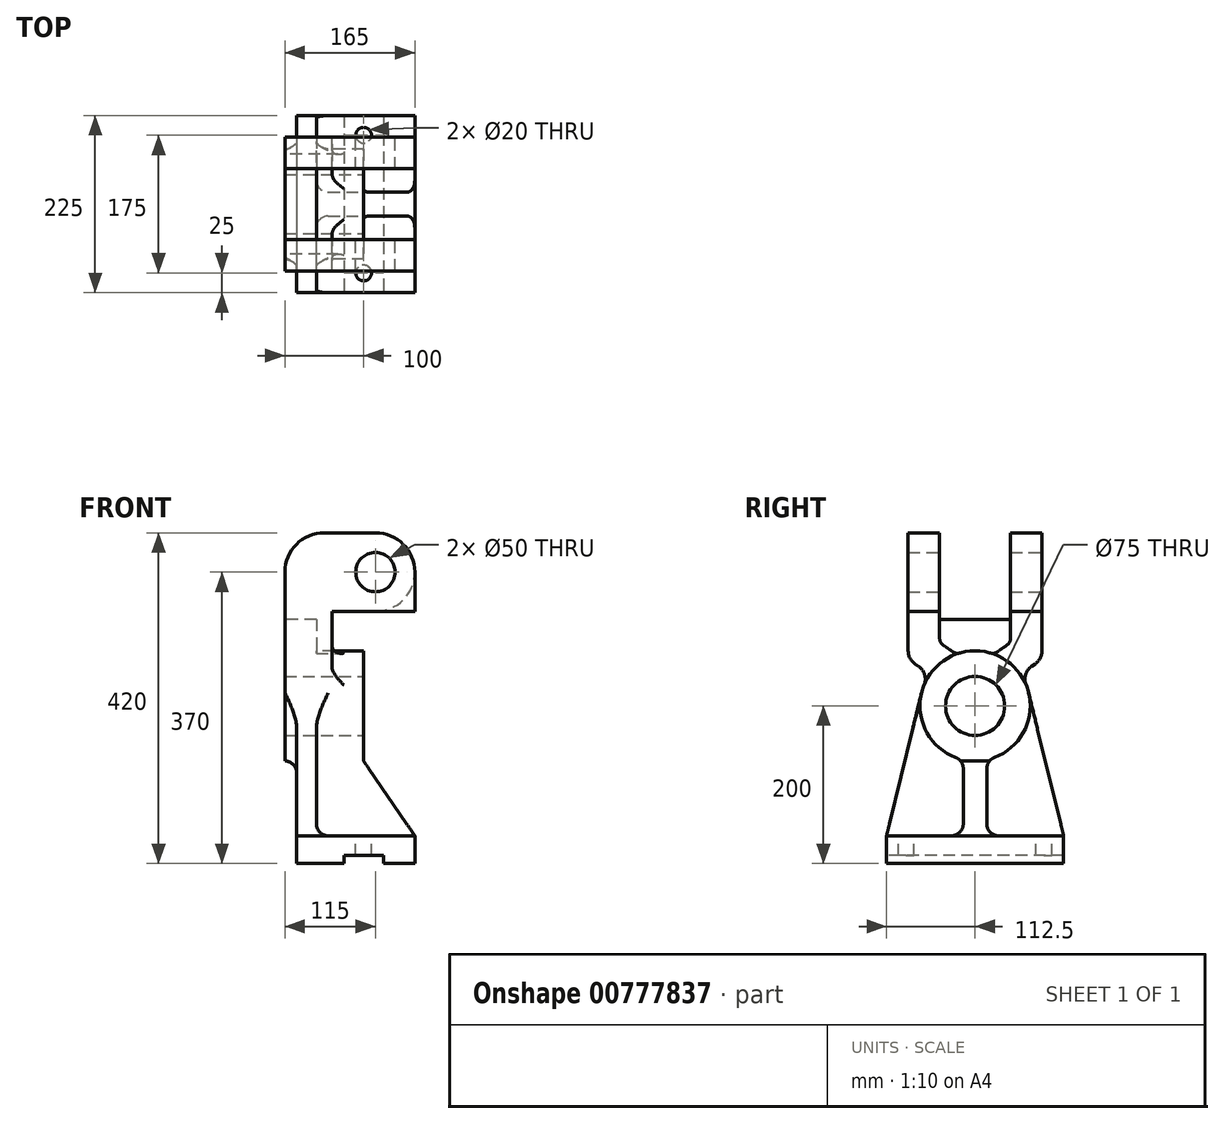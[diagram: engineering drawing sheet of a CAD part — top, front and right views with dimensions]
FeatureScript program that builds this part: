
annotation { "Feature Type Name" : "Feature", "Feature Type Description" : "" }
export const myFeature = defineFeature(function(context is Context, id is Id, definition is map)
    precondition{}
    {
        {
            var Q0;
            Q0=qCreatedBy(makeId("Right.planeOp"),FACE);
            var sketch = newSketch(context, id + "F0", { "sketchPlane" : qUnion([Q0])});
            skLineSegment(sketch, "E0", {"start": v(0, -200) * mm, "end": v(-112.5, -200) * mm});
            skLineSegment(sketch, "E1", {"start": v(-112.5, -200) * mm, "end": v(-112.5, -165) * mm});
            skLineSegment(sketch, "E2", {"start": v(-112.5, -165) * mm, "end": v(-67.99, 16.66) * mm});
            skLineSegment(sketch, "E3", {"start": v(-85, 70) * mm, "end": v(-85, 220) * mm});
            skLineSegment(sketch, "E4", {"start": v(-85, 220) * mm, "end": v(-45, 220) * mm});
            skLineSegment(sketch, "E5", {"start": v(-45, 220) * mm, "end": v(-45, 110) * mm});
            skLineSegment(sketch, "E6", {"start": v(-45, 110) * mm, "end": v(0, 110) * mm});
            skLineSegment(sketch, "E7", {"start": v(0, 110) * mm, "end": v(0, -200) * mm, "construction": true});
            skArc(sketch, "E8", {"start": v(-64.81, 26.45) * mm, "mid": v(-66.58, 21.61) * mm, "end": v(-67.99, 16.66) * mm});
            skLineSegment(sketch, "E9", {"start": v(-76.47, 53.62) * mm, "end": v(-71.86, 50.39) * mm});
            skPoint(sketch, "E10.visualSharp", {"position": v(-85, 59.59) * mm});
            skArc(sketch, "E10.filletArc", {"start": v(-85, 70) * mm, "mid": v(-82.74, 60.77) * mm, "end": v(-76.47, 53.62) * mm});
            skPoint(sketch, "E11.visualSharp", {"position": v(-57.3, 40.2) * mm});
            skArc(sketch, "E11.filletArc", {"start": v(-64.81, 26.45) * mm, "mid": v(-64.14, 39.65) * mm, "end": v(-71.86, 50.39) * mm});
            skLineSegment(sketch, "E12.MirrorCS", {"start": v(45, 110) * mm, "end": v(0, 110) * mm});
            skLineSegment(sketch, "E13.MirrorCS", {"start": v(45, 220) * mm, "end": v(45, 110) * mm});
            skLineSegment(sketch, "E14.MirrorCS", {"start": v(85, 220) * mm, "end": v(45, 220) * mm});
            skLineSegment(sketch, "E15.MirrorCS", {"start": v(85, 70) * mm, "end": v(85, 220) * mm});
            skArc(sketch, "E16.MirrorCS", {"start": v(85, 70) * mm, "mid": v(82.74, 60.77) * mm, "end": v(76.47, 53.62) * mm});
            skLineSegment(sketch, "E17.MirrorCS", {"start": v(76.47, 53.62) * mm, "end": v(71.86, 50.39) * mm});
            skArc(sketch, "E18.MirrorCS", {"start": v(64.81, 26.45) * mm, "mid": v(64.14, 39.65) * mm, "end": v(71.86, 50.39) * mm});
            skArc(sketch, "E19.MirrorCS", {"start": v(64.81, 26.45) * mm, "mid": v(66.58, 21.61) * mm, "end": v(67.99, 16.66) * mm});
            skLineSegment(sketch, "E20.MirrorCS", {"start": v(112.5, -165) * mm, "end": v(67.99, 16.66) * mm});
            skLineSegment(sketch, "E21.MirrorCS", {"start": v(112.5, -200) * mm, "end": v(112.5, -165) * mm});
            skLineSegment(sketch, "E22.MirrorCS", {"start": v(0, -200) * mm, "end": v(112.5, -200) * mm});
            skSolve(sketch);
        }
        {
            var Q0;
            Q0=makeQuery(id+"F0.imprint","IMPRINT",FACE,{"disambiguationData":[TD([[makeQuery(id+"F0.imprint","IMPRINT",EDGE,{"derivedFrom":sQuery(id+"F0.wireOp",EDGE,"E0")}),-1.0]])]});
            extrude(context, id + "F1", {"entities" : qUnion([Q0]), "depth" : 150 * mm, "offsetDistance" : 25 * mm, "hasSecondDirection" : true, "secondDirectionOppositeDirection" : true, "secondDirectionDepth" : 15 * mm});
        }
        {
            var Q0;
            Q0=makeQuery(id+"F1.opExtrude","CAP_FACE",FACE,{"disambiguationData":[OSD([sQuery(id+"F0.wireOp",EDGE,"E0"),sQuery(id+"F0.wireOp",EDGE,"E1"),sQuery(id+"F0.wireOp",EDGE,"E2"),sQuery(id+"F0.wireOp",EDGE,"E3"),sQuery(id+"F0.wireOp",EDGE,"E4"),sQuery(id+"F0.wireOp",EDGE,"E5"),sQuery(id+"F0.wireOp",EDGE,"E6"),sQuery(id+"F0.wireOp",EDGE,"E8"),sQuery(id+"F0.wireOp",EDGE,"E9"),sQuery(id+"F0.wireOp",EDGE,"E10.filletArc"),sQuery(id+"F0.wireOp",EDGE,"E11.filletArc"),sQuery(id+"F0.wireOp",EDGE,"E12.MirrorCS"),sQuery(id+"F0.wireOp",EDGE,"E13.MirrorCS"),sQuery(id+"F0.wireOp",EDGE,"E14.MirrorCS"),sQuery(id+"F0.wireOp",EDGE,"E15.MirrorCS"),sQuery(id+"F0.wireOp",EDGE,"E16.MirrorCS"),sQuery(id+"F0.wireOp",EDGE,"E17.MirrorCS"),sQuery(id+"F0.wireOp",EDGE,"E18.MirrorCS"),sQuery(id+"F0.wireOp",EDGE,"E19.MirrorCS"),sQuery(id+"F0.wireOp",EDGE,"E20.MirrorCS"),sQuery(id+"F0.wireOp",EDGE,"E21.MirrorCS"),sQuery(id+"F0.wireOp",EDGE,"E22.MirrorCS")])],"isStart":false});
            var sketch = newSketch(context, id + "F2", { "sketchPlane" : qUnion([Q0])});
            skLineSegment(sketch, "E23", {"start": v(-112.5, -165) * mm, "end": v(-30, -165) * mm});
            skLineSegment(sketch, "E24", {"start": v(-15, -150) * mm, "end": v(-15, -79.53) * mm});
            skArc(sketch, "E25", {"start": v(-67.99, 16.66) * mm, "mid": v(-61.93, -32.63) * mm, "end": v(-24.7, -65.5) * mm});
            skPoint(sketch, "E26.visualSharp", {"position": v(-15, -68.37) * mm});
            skArc(sketch, "E26.filletArc", {"start": v(-15, -79.53) * mm, "mid": v(-17.66, -71) * mm, "end": v(-24.7, -65.5) * mm});
            skPoint(sketch, "E27.visualSharp", {"position": v(-15, -165) * mm});
            skArc(sketch, "E27.filletArc", {"start": v(-30, -165) * mm, "mid": v(-19.4, -160.6) * mm, "end": v(-15, -150) * mm});
            skLineSegment(sketch, "E28", {"start": v(-112.5, -165) * mm, "end": v(-67.99, 16.66) * mm});
            skLineSegment(sketch, "E29", {"start": v(0, 128.7) * mm, "end": v(0, -232.35) * mm, "construction": true});
            skLineSegment(sketch, "E30.MirrorCS", {"start": v(112.5, -165) * mm, "end": v(67.99, 16.66) * mm});
            skArc(sketch, "E31.MirrorCS", {"start": v(67.99, 16.66) * mm, "mid": v(61.93, -32.63) * mm, "end": v(24.7, -65.5) * mm});
            skArc(sketch, "E32.MirrorCS", {"start": v(15, -79.53) * mm, "mid": v(17.66, -71) * mm, "end": v(24.7, -65.5) * mm});
            skLineSegment(sketch, "E33.MirrorCS", {"start": v(15, -150) * mm, "end": v(15, -79.53) * mm});
            skArc(sketch, "E34.MirrorCS", {"start": v(30, -165) * mm, "mid": v(19.4, -160.6) * mm, "end": v(15, -150) * mm});
            skLineSegment(sketch, "E35.MirrorCS", {"start": v(112.5, -165) * mm, "end": v(30, -165) * mm});
            skSolve(sketch);
        }
        {
            var Q0;
            Q0=makeQuery(id+"F2.imprint","IMPRINT",FACE,{"disambiguationData":[TD([[makeQuery(id+"F2.imprint","IMPRINT",EDGE,{"derivedFrom":sQuery(id+"F2.wireOp",EDGE,"E23")}),1.0]])]});
            var Q1;
            Q1=makeQuery(id+"F2.imprint","IMPRINT",FACE,{"disambiguationData":[TD([[makeQuery(id+"F2.imprint","IMPRINT",EDGE,{"derivedFrom":sQuery(id+"F2.wireOp",EDGE,"E30.MirrorCS")}),1.0]])]});
            extrude(context, id + "F3", {"entities" : qUnion([Q0, Q1]), "operationType" : NewBodyOperationType.REMOVE, "oppositeDirection" : true, "depth" : 125 * mm, "offsetDistance" : 25 * mm});
        }
        {
            var Q0;
            Q0=makeQuery(id+"F1.opExtrude","CAP_FACE",FACE,{"disambiguationData":[OSD([sQuery(id+"F0.wireOp",EDGE,"E0"),sQuery(id+"F0.wireOp",EDGE,"E1"),sQuery(id+"F0.wireOp",EDGE,"E2"),sQuery(id+"F0.wireOp",EDGE,"E3"),sQuery(id+"F0.wireOp",EDGE,"E4"),sQuery(id+"F0.wireOp",EDGE,"E5"),sQuery(id+"F0.wireOp",EDGE,"E6"),sQuery(id+"F0.wireOp",EDGE,"E8"),sQuery(id+"F0.wireOp",EDGE,"E9"),sQuery(id+"F0.wireOp",EDGE,"E10.filletArc"),sQuery(id+"F0.wireOp",EDGE,"E11.filletArc"),sQuery(id+"F0.wireOp",EDGE,"E12.MirrorCS"),sQuery(id+"F0.wireOp",EDGE,"E13.MirrorCS"),sQuery(id+"F0.wireOp",EDGE,"E14.MirrorCS"),sQuery(id+"F0.wireOp",EDGE,"E15.MirrorCS"),sQuery(id+"F0.wireOp",EDGE,"E16.MirrorCS"),sQuery(id+"F0.wireOp",EDGE,"E17.MirrorCS"),sQuery(id+"F0.wireOp",EDGE,"E18.MirrorCS"),sQuery(id+"F0.wireOp",EDGE,"E19.MirrorCS"),sQuery(id+"F0.wireOp",EDGE,"E20.MirrorCS"),sQuery(id+"F0.wireOp",EDGE,"E21.MirrorCS"),sQuery(id+"F0.wireOp",EDGE,"E22.MirrorCS")])],"isStart":false});
            var sketch = newSketch(context, id + "F4", { "sketchPlane" : qUnion([Q0])});
            skArc(sketch, "E36", {"start": v(-64.81, 26.45) * mm, "mid": v(0, 70) * mm, "end": v(64.81, 26.45) * mm});
            skLineSegment(sketch, "E37", {"start": v(-85, 120) * mm, "end": v(-45, 120) * mm});
            skLineSegment(sketch, "E38", {"start": v(45, 120) * mm, "end": v(85, 120) * mm});
            skLineSegment(sketch, "E39", {"start": v(-45, 120) * mm, "end": v(-45, 110) * mm});
            skLineSegment(sketch, "E40", {"start": v(-45, 110) * mm, "end": v(45, 110) * mm});
            skLineSegment(sketch, "E41", {"start": v(45, 110) * mm, "end": v(45, 120) * mm});
            skLineSegment(sketch, "E42", {"start": v(85, 120) * mm, "end": v(85, 70) * mm});
            skLineSegment(sketch, "E43", {"start": v(-85, 120) * mm, "end": v(-85, 70) * mm});
            skArc(sketch, "E44.0", {"start": v(-85, 70) * mm, "mid": v(-82.74, 60.77) * mm, "end": v(-76.47, 53.62) * mm});
            skLineSegment(sketch, "E45.0", {"start": v(-76.47, 53.62) * mm, "end": v(-71.86, 50.39) * mm});
            skArc(sketch, "E46.0", {"start": v(-64.81, 26.45) * mm, "mid": v(-64.14, 39.65) * mm, "end": v(-71.86, 50.39) * mm});
            skArc(sketch, "E47.0.13", {"start": v(64.81, 26.45) * mm, "mid": v(64.14, 39.65) * mm, "end": v(71.86, 50.39) * mm});
            skLineSegment(sketch, "E47.0.14", {"start": v(71.86, 50.39) * mm, "end": v(76.47, 53.62) * mm});
            skArc(sketch, "E47.0.15", {"start": v(76.47, 53.62) * mm, "mid": v(82.74, 60.77) * mm, "end": v(85, 70) * mm});
            skLineSegment(sketch, "E47.0.16", {"start": v(85, 70) * mm, "end": v(85, 120) * mm});
            skLineSegment(sketch, "E47.0.18", {"start": v(45, 120) * mm, "end": v(45, 110) * mm});
            skLineSegment(sketch, "E47.0.19", {"start": v(45, 110) * mm, "end": v(-45, 110) * mm});
            skLineSegment(sketch, "E47.0.20", {"start": v(-45, 110) * mm, "end": v(-45, 120) * mm});
            skArc(sketch, "E47.0.25", {"start": v(-71.86, 50.39) * mm, "mid": v(-64.14, 39.65) * mm, "end": v(-64.81, 26.45) * mm});
            skSolve(sketch);
        }
        {
            var Q0;
            Q0 = qSketchRegion(id + "F4", true);
            extrude(context, id + "F5", {"entities" : qUnion([Q0]), "operationType" : NewBodyOperationType.REMOVE, "oppositeDirection" : true, "depth" : 105 * mm, "offsetDistance" : 25 * mm});
        }
        {
            var Q0;
            Q0=qCreatedBy(makeId("Front.planeOp"),FACE);
            var sketch = newSketch(context, id + "F6", { "sketchPlane" : qUnion([Q0])});
            skLineSegment(sketch, "E48", {"start": v(85, 70) * mm, "end": v(85, -70) * mm});
            skLineSegment(sketch, "E49", {"start": v(85, -70) * mm, "end": v(150, -165) * mm});
            skLineSegment(sketch, "E50", {"start": v(150, -165) * mm, "end": v(150, -200) * mm});
            skLineSegment(sketch, "E51", {"start": v(150, -200) * mm, "end": v(160, -200) * mm});
            skLineSegment(sketch, "E52", {"start": v(160, -200) * mm, "end": v(160, 70) * mm});
            skLineSegment(sketch, "E53", {"start": v(160, 70) * mm, "end": v(85, 70) * mm});
            skSolve(sketch);
        }
        {
            var Q0;
            Q0=makeQuery(id+"F6.imprint","IMPRINT",FACE,{"disambiguationData":[TD([[makeQuery(id+"F6.imprint","IMPRINT",EDGE,{"derivedFrom":sQuery(id+"F6.wireOp",EDGE,"E48")}),1.0]])]});
            extrude(context, id + "F7", {"entities" : qUnion([Q0]), "operationType" : NewBodyOperationType.REMOVE, "endBound" : BoundingType.SYMMETRIC, "oppositeDirection" : true, "depth" : 225 * mm, "offsetDistance" : 25 * mm});
        }
        {
            var Q0;
            Q0=makeQuery(id+"F1.opExtrude","CAP_EDGE",EDGE,{"disambiguationData":[OSD([sQuery(id+"F0.wireOp",EDGE,"E4")])],"isStart":false});
            var Q1;
            Q1=makeQuery(id+"F1.opExtrude","CAP_EDGE",EDGE,{"disambiguationData":[OSD([sQuery(id+"F0.wireOp",EDGE,"E14.MirrorCS")])],"isStart":false});
            var Q2;
            Q2=makeQuery(id+"F5.boolean.opBoolean","COPY",EDGE,{"derivedFrom":makeQuery(id+"F5.opExtrude","CAP_EDGE",EDGE,{"disambiguationData":[OSD([sQuery(id+"F4.wireOp",EDGE,"E38")])],"isStart":true})});
            var Q3;
            Q3=makeQuery(id+"F5.boolean.opBoolean","COPY",EDGE,{"derivedFrom":makeQuery(id+"F5.opExtrude","CAP_EDGE",EDGE,{"disambiguationData":[OSD([sQuery(id+"F4.wireOp",EDGE,"E37")])],"isStart":true})});
            var Q4;
            Q4=makeQuery(id+"F1.opExtrude","CAP_EDGE",EDGE,{"disambiguationData":[OSD([sQuery(id+"F0.wireOp",EDGE,"E4")])],"isStart":true});
            var Q5;
            Q5=makeQuery(id+"F1.opExtrude","CAP_EDGE",EDGE,{"disambiguationData":[OSD([sQuery(id+"F0.wireOp",EDGE,"E14.MirrorCS")])],"isStart":true});
            fillet(context, id + "F8", {"entities" : qUnion([Q0, Q1, Q2, Q3, Q4, Q5]), "radius" : 50 * mm, "tangentPropagation" : true, "allowEdgeOverflow" : false});
        }
        {
            var Q0;
            Q0=makeQuery(id+"F5.boolean.opBoolean","COPY",FACE,{"derivedFrom":makeQuery(id+"F5.opExtrude","CAP_FACE",FACE,{"disambiguationData":[OSD([sQuery(id+"F4.wireOp",EDGE,"E36"),sQuery(id+"F4.wireOp",EDGE,"E37"),sQuery(id+"F4.wireOp",EDGE,"E38"),sQuery(id+"F4.wireOp",EDGE,"E47.0.13"),sQuery(id+"F4.wireOp",EDGE,"E47.0.14"),sQuery(id+"F4.wireOp",EDGE,"E47.0.15"),sQuery(id+"F4.wireOp",EDGE,"E47.0.16"),sQuery(id+"F4.wireOp",EDGE,"E47.0.18"),sQuery(id+"F4.wireOp",EDGE,"E47.0.19"),sQuery(id+"F4.wireOp",EDGE,"E47.0.20"),sQuery(id+"F4.wireOp",EDGE,"E43"),sQuery(id+"F4.wireOp",EDGE,"E44.0"),sQuery(id+"F4.wireOp",EDGE,"E45.0"),sQuery(id+"F4.wireOp",EDGE,"E47.0.25")])],"isStart":false})});
            var sketch = newSketch(context, id + "F9", { "sketchPlane" : qUnion([Q0])});
            skLineSegment(sketch, "E54", {"start": v(-45, 110) * mm, "end": v(-45, 85.62) * mm});
            skLineSegment(sketch, "E55", {"start": v(-40.74, 77.43) * mm, "end": v(-28.14, 68.6) * mm});
            skPoint(sketch, "E56.visualSharp", {"position": v(-45, 80.41) * mm});
            skArc(sketch, "E56.filletArc", {"start": v(-45, 85.62) * mm, "mid": v(-43.87, 81) * mm, "end": v(-40.74, 77.43) * mm});
            skArc(sketch, "E57", {"start": v(-19.6, 67.2) * mm, "mid": v(0, 70) * mm, "end": v(19.6, 67.2) * mm});
            skPoint(sketch, "E58.visualSharp", {"position": v(-24.05, 65.74) * mm});
            skArc(sketch, "E58.filletArc", {"start": v(-28.14, 68.6) * mm, "mid": v(-24.03, 66.93) * mm, "end": v(-19.6, 67.2) * mm});
            skLineSegment(sketch, "E59", {"start": v(0, 125.73) * mm, "end": v(0, 0) * mm, "construction": true});
            skArc(sketch, "E60.MirrorCS", {"start": v(28.14, 68.6) * mm, "mid": v(24.03, 66.93) * mm, "end": v(19.6, 67.2) * mm});
            skLineSegment(sketch, "E61.MirrorCS", {"start": v(40.74, 77.43) * mm, "end": v(28.14, 68.6) * mm});
            skArc(sketch, "E62.MirrorCS", {"start": v(45, 85.62) * mm, "mid": v(43.87, 81) * mm, "end": v(40.74, 77.43) * mm});
            skLineSegment(sketch, "E63.MirrorCS", {"start": v(45, 110) * mm, "end": v(45, 85.62) * mm});
            skLineSegment(sketch, "E64", {"start": v(-45, 110) * mm, "end": v(45, 110) * mm});
            skSolve(sketch);
        }
        {
            var Q0;
            Q0=makeQuery(id+"F9.imprint","IMPRINT",FACE,{"disambiguationData":[TD([[makeQuery(id+"F9.imprint","IMPRINT",EDGE,{"derivedFrom":sQuery(id+"F9.wireOp",EDGE,"E54")}),1.0]])]});
            extrude(context, id + "F10", {"entities" : qUnion([Q0]), "operationType" : NewBodyOperationType.REMOVE, "oppositeDirection" : true, "depth" : 20 * mm, "offsetDistance" : 25 * mm});
        }
        {
            var Q0;
            Q0=makeQuery(id+"F1.opExtrude","CAP_FACE",FACE,{"disambiguationData":[OSD([sQuery(id+"F0.wireOp",EDGE,"E0"),sQuery(id+"F0.wireOp",EDGE,"E1"),sQuery(id+"F0.wireOp",EDGE,"E2"),sQuery(id+"F0.wireOp",EDGE,"E3"),sQuery(id+"F0.wireOp",EDGE,"E4"),sQuery(id+"F0.wireOp",EDGE,"E5"),sQuery(id+"F0.wireOp",EDGE,"E6"),sQuery(id+"F0.wireOp",EDGE,"E8"),sQuery(id+"F0.wireOp",EDGE,"E9"),sQuery(id+"F0.wireOp",EDGE,"E10.filletArc"),sQuery(id+"F0.wireOp",EDGE,"E11.filletArc"),sQuery(id+"F0.wireOp",EDGE,"E12.MirrorCS"),sQuery(id+"F0.wireOp",EDGE,"E13.MirrorCS"),sQuery(id+"F0.wireOp",EDGE,"E14.MirrorCS"),sQuery(id+"F0.wireOp",EDGE,"E15.MirrorCS"),sQuery(id+"F0.wireOp",EDGE,"E16.MirrorCS"),sQuery(id+"F0.wireOp",EDGE,"E17.MirrorCS"),sQuery(id+"F0.wireOp",EDGE,"E18.MirrorCS"),sQuery(id+"F0.wireOp",EDGE,"E19.MirrorCS"),sQuery(id+"F0.wireOp",EDGE,"E20.MirrorCS"),sQuery(id+"F0.wireOp",EDGE,"E21.MirrorCS"),sQuery(id+"F0.wireOp",EDGE,"E22.MirrorCS")])],"isStart":true});
            var sketch = newSketch(context, id + "F11", { "sketchPlane" : qUnion([Q0])});
            skArc(sketch, "E65", {"start": v(-67.99, 16.66) * mm, "mid": v(0, -70) * mm, "end": v(67.99, 16.66) * mm});
            skLineSegment(sketch, "E66", {"start": v(-67.99, 16.66) * mm, "end": v(-112.5, -165) * mm});
            skLineSegment(sketch, "E67", {"start": v(-112.5, -165) * mm, "end": v(-112.5, -200) * mm});
            skLineSegment(sketch, "E68", {"start": v(-112.5, -200) * mm, "end": v(112.5, -200) * mm});
            skLineSegment(sketch, "E69", {"start": v(112.5, -200) * mm, "end": v(112.5, -165) * mm});
            skLineSegment(sketch, "E70", {"start": v(112.5, -165) * mm, "end": v(67.99, 16.66) * mm});
            skSolve(sketch);
        }
        {
            var Q0;
            Q0=makeQuery(id+"F11.imprint","IMPRINT",FACE,{"disambiguationData":[TD([[makeQuery(id+"F11.imprint","IMPRINT",EDGE,{"derivedFrom":sQuery(id+"F11.wireOp",EDGE,"E65")}),-1.0]])]});
            extrude(context, id + "F12", {"entities" : qUnion([Q0]), "operationType" : NewBodyOperationType.REMOVE, "oppositeDirection" : true, "depth" : 15 * mm, "offsetDistance" : 25 * mm});
        }
        {
            var Q0;
            Q0=makeQuery(id+"F7.boolean.opBoolean","COPY",FACE,{"derivedFrom":makeQuery(id+"F7.opExtrude","SWEPT_FACE",FACE,{"disambiguationData":[OSD([sQuery(id+"F6.wireOp",EDGE,"E48")])]})});
            var sketch = newSketch(context, id + "F13", { "sketchPlane" : qUnion([Q0])});
            skCircle(sketch, "E71", {"center": v(0, 0) * mm, "radius": 37.5 * mm});
            skSolve(sketch);
        }
        {
            var Q0;
            Q0=makeQuery(id+"F13.imprint","IMPRINT",FACE,{"disambiguationData":[TD([[makeQuery(id+"F13.imprint","IMPRINT",EDGE,{"derivedFrom":sQuery(id+"F13.wireOp",EDGE,"E71")}),1.0]])]});
            extrude(context, id + "F14", {"entities" : qUnion([Q0]), "operationType" : NewBodyOperationType.REMOVE, "oppositeDirection" : true, "depth" : 100 * mm, "offsetDistance" : 25 * mm});
        }
        {
            var Q0;
            Q0=makeQuery(id+"F1.opExtrude","SWEPT_FACE",FACE,{"disambiguationData":[OSD([sQuery(id+"F0.wireOp",EDGE,"E15.MirrorCS")])]});
            var sketch = newSketch(context, id + "F15", { "sketchPlane" : qUnion([Q0])});
            skCircle(sketch, "E72", {"center": v(-100, 170) * mm, "radius": 25 * mm});
            skSolve(sketch);
        }
        {
            var Q0;
            Q0=makeQuery(id+"F15.imprint","IMPRINT",FACE,{"disambiguationData":[TD([[makeQuery(id+"F15.imprint","IMPRINT",EDGE,{"derivedFrom":sQuery(id+"F15.wireOp",EDGE,"E72")}),1.0]])]});
            extrude(context, id + "F16", {"entities" : qUnion([Q0]), "operationType" : NewBodyOperationType.REMOVE, "oppositeDirection" : true, "depth" : 170 * mm, "offsetDistance" : 25 * mm});
        }
        {
            var Q0;
            Q0=makeQuery(id+"F3.boolean.opBoolean","COPY",FACE,{"derivedFrom":makeQuery(id+"F3.opExtrude","SWEPT_FACE",FACE,{"disambiguationData":[OSD([sQuery(id+"F2.wireOp",EDGE,"E23")])]})});
            var sketch = newSketch(context, id + "F17", { "sketchPlane" : qUnion([Q0])});
            skCircle(sketch, "E73", {"center": v(85, 87.5) * mm, "radius": 10 * mm});
            skCircle(sketch, "E74", {"center": v(85, -87.5) * mm, "radius": 10 * mm});
            skSolve(sketch);
        }
        {
            var Q0;
            Q0=makeQuery(id+"F17.imprint","IMPRINT",FACE,{"disambiguationData":[TD([[makeQuery(id+"F17.imprint","IMPRINT",EDGE,{"derivedFrom":sQuery(id+"F17.wireOp",EDGE,"E74")}),1.0]])]});
            var Q1;
            Q1=makeQuery(id+"F17.imprint","IMPRINT",FACE,{"disambiguationData":[TD([[makeQuery(id+"F17.imprint","IMPRINT",EDGE,{"derivedFrom":sQuery(id+"F17.wireOp",EDGE,"E73")}),1.0]])]});
            extrude(context, id + "F18", {"entities" : qUnion([Q0, Q1]), "operationType" : NewBodyOperationType.REMOVE, "oppositeDirection" : true, "depth" : 35 * mm, "offsetDistance" : 25 * mm});
        }
        {
            var Q0;
            Q0=qCreatedBy(makeId("Front.planeOp"),FACE);
            var sketch = newSketch(context, id + "F19", { "sketchPlane" : qUnion([Q0])});
            skLineSegment(sketch, "E75.bottom", {"start": v(60, -200) * mm, "end": v(110, -200) * mm});
            skLineSegment(sketch, "E75.top", {"start": v(60, -190) * mm, "end": v(110, -190) * mm});
            skLineSegment(sketch, "E75.left", {"start": v(60, -200) * mm, "end": v(60, -190) * mm});
            skLineSegment(sketch, "E75.right", {"start": v(110, -200) * mm, "end": v(110, -190) * mm});
            skSolve(sketch);
        }
        {
            var Q0;
            Q0 = qSketchRegion(id + "F19", true);
            extrude(context, id + "F20", {"entities" : qUnion([Q0]), "operationType" : NewBodyOperationType.REMOVE, "endBound" : BoundingType.SYMMETRIC, "oppositeDirection" : true, "depth" : 225 * mm, "offsetDistance" : 25 * mm});
        }
        {
            var Q0;
            Q0=makeQuery(id+"F3.boolean.opBoolean","COPY",EDGE,{"derivedFrom":makeQuery(id+"F3.opExtrude","CAP_EDGE",EDGE,{"disambiguationData":[OSD([sQuery(id+"F2.wireOp",EDGE,"E23")])],"isStart":false})});
            var Q1;
            Q1=makeQuery(id+"F3.boolean.opBoolean","COPY",EDGE,{"derivedFrom":makeQuery(id+"F3.opExtrude","CAP_EDGE",EDGE,{"disambiguationData":[OSD([sQuery(id+"F2.wireOp",EDGE,"E35.MirrorCS")])],"isStart":false})});
            var Q2;
            {var subQ0=sQuery(id+"F4.wireOp",EDGE,"E36");Q2=makeQuery(id+"F10.boolean.opBoolean","SPLIT",EDGE,{"disambiguationData":[TD([makeQuery(id+"F1.opExtrude","SWEPT_FACE",FACE,{"disambiguationData":[OSD([sQuery(id+"F0.wireOp",EDGE,"E11.filletArc")])]})])],"derivedFrom":makeQuery(id+"F5.boolean.opBoolean","COPY",EDGE,{"derivedFrom":makeQuery(id+"F5.opExtrude","CAP_EDGE",EDGE,{"disambiguationData":[OSD([subQ0])],"isStart":false})})});}
            var Q3;
            {var subQ0=sQuery(id+"F4.wireOp",EDGE,"E36");Q3=makeQuery(id+"F10.boolean.opBoolean","SPLIT",EDGE,{"disambiguationData":[TD([makeQuery(id+"F1.opExtrude","SWEPT_FACE",FACE,{"disambiguationData":[OSD([sQuery(id+"F0.wireOp",EDGE,"E18.MirrorCS")])]})])],"derivedFrom":makeQuery(id+"F5.boolean.opBoolean","COPY",EDGE,{"derivedFrom":makeQuery(id+"F5.opExtrude","CAP_EDGE",EDGE,{"disambiguationData":[OSD([subQ0])],"isStart":false})})});}
            var Q4;
            Q4=makeQuery(id+"F12.boolean.opBoolean","COPY",EDGE,{"derivedFrom":makeQuery(id+"F12.opExtrude","CAP_EDGE",EDGE,{"disambiguationData":[OSD([sQuery(id+"F11.wireOp",EDGE,"E65")])],"isStart":false})});
            fillet(context, id + "F21", {"entities" : qUnion([Q0, Q1, Q2, Q3, Q4]), "radius" : 15 * mm, "tangentPropagation" : true, "allowEdgeOverflow" : false});
        }
    });
